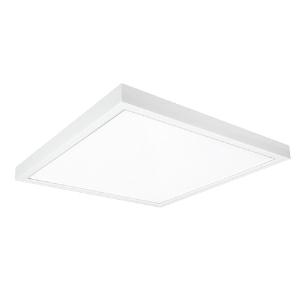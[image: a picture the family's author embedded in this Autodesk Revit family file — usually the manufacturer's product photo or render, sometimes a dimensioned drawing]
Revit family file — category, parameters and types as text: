
# Revit family: 3f_filippi_-_p_250_luce_diffusa_lgs_3f_filippi_-_10048_-_p_250_28w_led_lgs_596x596
name_source: partatom
category: Lighting Fixtures
units: mm (PartAtom-declared; Revit-internal decimal feet)

## family parameters
Cut with Voids When Loaded = No
Host = Face
Light Source = No
Part Type = Normal
Room Calculation Point = No
Round Connector Dimension = Use Diameter
Shared = No

## types (1)
- 3F Filippi - P 250 Luce Diffusa LGS (1 x LED, 3707 lm, 31 W, 4000 K)
    Apparent Load = 31 VA
    Approval mark = ENEC
    CIE Flux Codes = 66 93 99 100 100
    Color Rendering = 80
    Color Temperature = 4000 K
    Control Gear = Electronic ballast
    Default Elevation = 1800 mm
    Description = ILLUMINOTECHNICAL
Luminous efficiency 100% (DLOR 100%, ULOR 0%).
Initial luminous flux of the luminaire 3707 lm.
Direct symmetric distribution.
Installation Interdistance Transv.D = 1.18 x hu - Long.D = 1.17 x hu.
Average luminance <1500 cd/m² for radial angles >65°.
Tabular UGR (CIE 117 - 4H-8H; S=0.25H; 70/50/20): RUG 16.5 - 16.5.
Beam angle: 87° - 86°.
Luminous efficacy 120 lm/W.
Lifetime (L93/B10): 30000 h. (tq+25°C)
Lifetime (L90/B10): 50000 h. (tq+25°C)
Lifetime (L85/B10): 80000 h. (tq+25°C)
Lifetime (L80/B10): 100000 h. (tq+25°C)
Sudden decreased luminous flux after 50000 hours: 0% (C0).
Photobiological safety in compliance with IEC/TR 62778: RG0 risk exempt, (IEC 62471).
In compliance with IEC/EN 62722-2-1 - IEC/EN 62717 standards.

SOURCE
Squared LED module 28W/840.
Energy efficiency class (UE 2019/2020 - UE 2019/2015): D.
CIE 13.3 Colour rendering index: CRI >80 (R9 <50%).
IES TM-30 Fidelity Index: Rf = 84 Rg = 95.
CCT nominal colour temperature 4000 K.
Colour initial tolerance (MacAdam): SDCM 3.

MECHANICAL
Housing in galvannealed steel, painted in white epoxy-polyester.
Height only 55 mm.
LGS micro-prismatic flat diffuser in transparent methacrylate (PMMA), multi-lenticular exterior, anti-glare, locked to the white painted aluminium perimeter frame, hinged opening.
Anti-glare opal polycarbonate filter for brightness uniformity.
Luminaire with limited surface temperature. - D - (EN 60598-2-24)
Dimensions: 596x596 mm, height 55 mm. Weight 5.38 kg.
IP40 protection degree.
Mechanical strength to impacts IK06 (1 joule).
Glow-wire test resistance 650°C.

ELECTRICAL
Halogen Free electronic wiring 230V-50/60Hz, power factor 0.95, THD <25%, constant output current, SELV, class I, 1 driver.
Power of the luminaire 31 W.
CE - IEC 60598-1 - EN 60598-1.
SAFE FLICKER: PstLM=<1 and SVM=<0.4 (IEC TR 61547-1 and IEC TR 63158), to ensure a more comfortable and safe light.
Luminaire compliant with EN 60598-2-22 for power supply from a centralised emergency system CPSS (Central Power Supply System), not incorporated in the luminaire - high risk areas excluded. The default power and flux are 100% in AC and 100% in DC.
Ambient temperature from 0°C to +25°C.
Temperature class T6 max 85°C.
Relative humidity UR: <85%.

INSTALLATION
Ceiling.
All accessories dedicated to this product are available on the Catalog and on our website www.3F-Filippi.com.

APPLICATIONS
Particularly suitable for low height environments.
Environments: with video terminals, representative areas, offices.
Environments with exacting visual tasks, where diffused soft light for optimum visual comfort is required.

WARNING
Luminaire designed for disposal/recycling at end-of-life.
Replaceable (LED only) light source by a professional. Replaceable control gear by a professional.
    Height = 55 mm
    Lamp = 1 x LED
    Lamp Light Flux = 3707 lm
    Lamp Power = 31 W
    Lamp count = 1
    Length = 596 mm
    Lifetime = 50000 h
    Luminous efficacy = 120 lm/W
    Manufacturer = 3F Filippi
    ModVariant = No
    Model = 3F Filippi - 10048 - P 250 28W LED LGS 596x596
    Mounting Place = Ceiling
    Mounting Type = Surface mounted
    Number of Poles = 1
    OnlyDefault = Yes
    Power Factor = 1
    Product Name = 3F Filippi - P 250 Luce Diffusa LGS
    Product group = ceiling mounted luminaire
    ProductGroupID = 3
    Protection Class = Protection class I
    Protection Degree = IP 40
    RLX_Detail_Level = 1
    RLX_Emergency_Light_Flux = 0 lm
    RLX_Emergency_Type = 0
    RLX_Emergency_Type_DB = No
    RlxData = <blob elided: 34477 chars, md5=0d9a33dc>
    Socket = socket
    Standby Power = 0 W
    System Light Flux = 3707 lm
    System Power = 31 W
    Type Comments = Product without accessories
    Type Image = 3ffilippi_p_250_led_luce_diffusa_lgs.jpg
    URL = http://relux.com
    VarID = ---
    Voltage = 0 V
    Weight = 0.00 kg
    Width = 596 mm

## geometry (parser evidence)
native form markers: Blend x4, Sweep x11
no freeform markers — native parametric forms only
